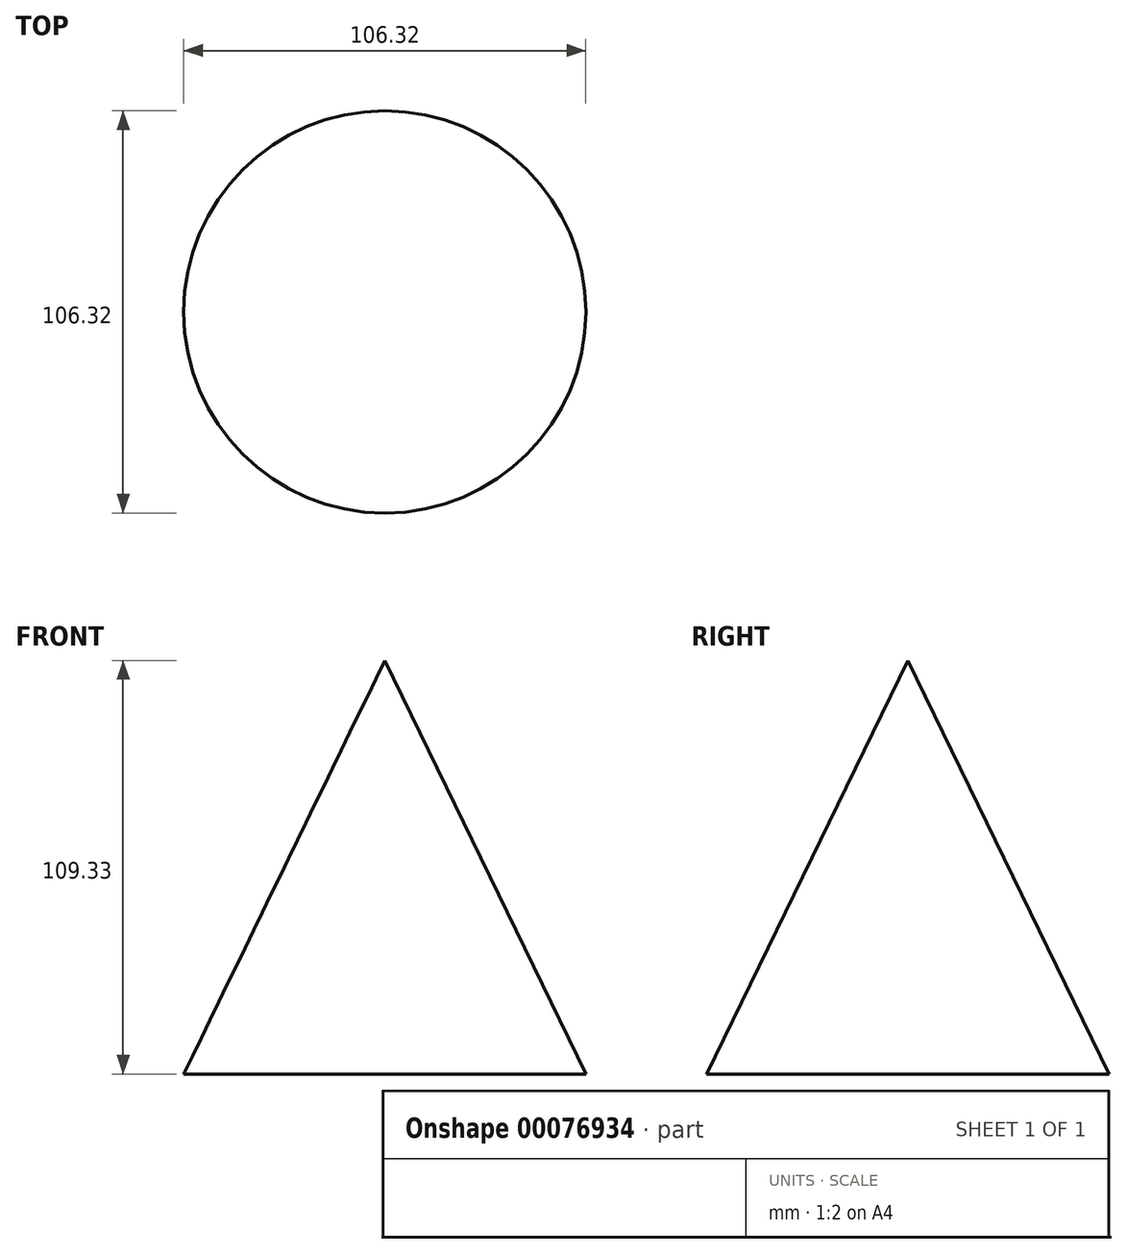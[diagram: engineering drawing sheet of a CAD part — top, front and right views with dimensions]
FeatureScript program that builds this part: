
annotation { "Feature Type Name" : "Feature", "Feature Type Description" : "" }
export const myFeature = defineFeature(function(context is Context, id is Id, definition is map)
    precondition{}
    {
        {
            var Q0;
            Q0=qCreatedBy(makeId("Front.planeOp"),FACE);
            var sketch = newSketch(context, id + "F0", { "sketchPlane" : qUnion([Q0])});
            skLineSegment(sketch, "E0", {"start": v(0, -41.24) * mm, "end": v(53.16, -41.24) * mm});
            skLineSegment(sketch, "E1", {"start": v(53.16, -41.24) * mm, "end": v(0, 68.09) * mm});
            skLineSegment(sketch, "E2", {"start": v(0, 68.09) * mm, "end": v(0, -41.24) * mm});
            skSolve(sketch);
        }
        {
            var Q0;
            Q0 = qSketchRegion(id + "F0", true);
            var Q1;
            Q1=sQuery(id+"F0.wireOp",EDGE,"E2");
            revolve(context, id + "F1", {"entities" : qUnion([Q0]), "axis" : qUnion([Q1]), "revolveType" : RevolveType.FULL});
        }
    });
